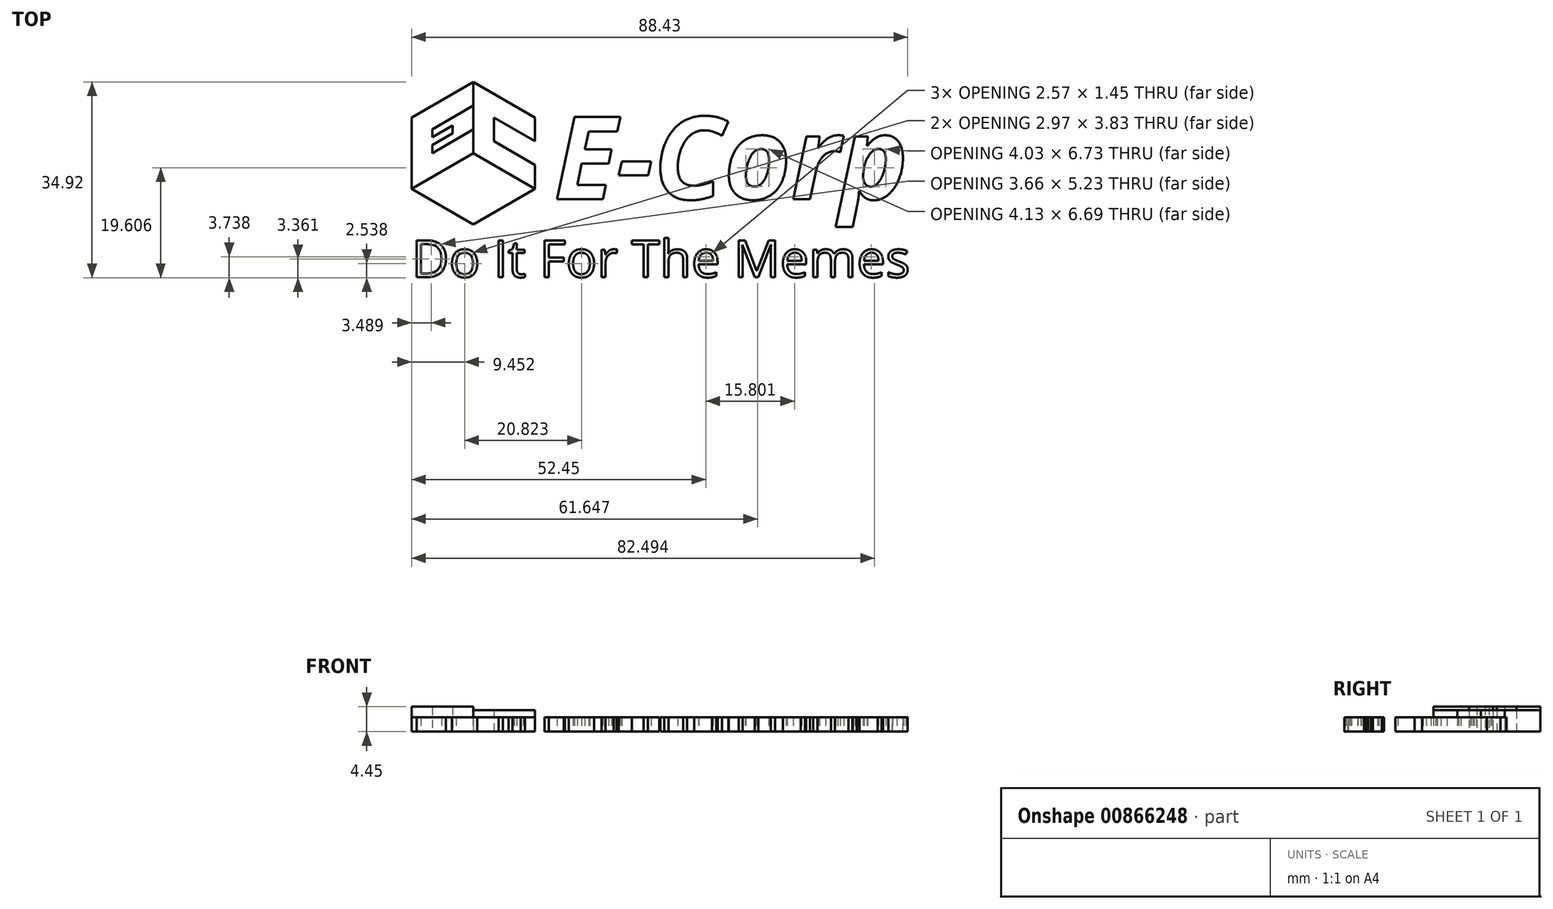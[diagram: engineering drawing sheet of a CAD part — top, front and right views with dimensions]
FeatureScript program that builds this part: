
annotation { "Feature Type Name" : "Feature", "Feature Type Description" : "" }
export const myFeature = defineFeature(function(context is Context, id is Id, definition is map)
    precondition{}
    {
        {
            var Q0;
            Q0=qCreatedBy(makeId("Top.planeOp"),FACE);
            var sketch = newSketch(context, id + "F0", { "sketchPlane" : qUnion([Q0])});
            skCircle(sketch, "E0.cCircle", {"center": v(-33.45, 15.53) * mm, "radius": 12.7 * mm, "construction": true});
            skLineSegment(sketch, "E0.0", {"start": v(-33.45, 28.23) * mm, "end": v(-22.45, 21.88) * mm});
            skLineSegment(sketch, "E0.1", {"start": v(-22.45, 21.88) * mm, "end": v(-22.45, 9.18) * mm});
            skLineSegment(sketch, "E0.2", {"start": v(-22.45, 9.18) * mm, "end": v(-33.45, 2.83) * mm});
            skLineSegment(sketch, "E0.3", {"start": v(-33.45, 2.83) * mm, "end": v(-44.45, 9.18) * mm});
            skLineSegment(sketch, "E0.4", {"start": v(-44.45, 9.18) * mm, "end": v(-44.45, 21.88) * mm});
            skLineSegment(sketch, "E0.5", {"start": v(-44.45, 21.88) * mm, "end": v(-33.45, 28.23) * mm});
            skText(sketch, "E1", { "text": "E-Corp", "fontName": "OpenSans-BoldItalic.ttf"});
            skText(sketch, "E2", { "text": "Do It For The Memes", "fontName": "OpenSans-Regular.ttf"});
            skLineSegment(sketch, "E3", {"start": v(-33.45, 15.53) * mm, "end": v(-44.45, 9.18) * mm});
            skLineSegment(sketch, "E4", {"start": v(-22.45, 9.18) * mm, "end": v(-33.45, 15.53) * mm});
            skLineSegment(sketch, "E5", {"start": v(-33.45, 15.53) * mm, "end": v(-33.45, 28.23) * mm});
            skLineSegment(sketch, "E6", {"start": v(-33.45, 19.76) * mm, "end": v(-40.78, 15.53) * mm});
            skLineSegment(sketch, "E7", {"start": v(-33.45, 19.76) * mm, "end": v(-33.45, 24) * mm});
            skLineSegment(sketch, "E8", {"start": v(-40.78, 19.76) * mm, "end": v(-33.45, 24) * mm});
            skLineSegment(sketch, "E9", {"start": v(-37.12, 13.41) * mm, "end": v(-40.78, 11.3) * mm});
            skLineSegment(sketch, "E10", {"start": v(-40.78, 15.53) * mm, "end": v(-40.78, 16.94) * mm});
            skPoint(sketch, "E11", {"position": v(-33.45, 21.88) * mm});
            skPoint(sketch, "E12", {"position": v(-38.95, 12.35) * mm});
            skLineSegment(sketch, "E13", {"start": v(-40.78, 18.35) * mm, "end": v(-37.12, 20.47) * mm});
            skLineSegment(sketch, "E14", {"start": v(-33.45, 22.58) * mm, "end": v(-33.45, 21.17) * mm});
            skLineSegment(sketch, "E15", {"start": v(-37.12, 19.06) * mm, "end": v(-40.78, 16.94) * mm});
            skLineSegment(sketch, "E16", {"start": v(-29.79, 17.64) * mm, "end": v(-29.79, 21.88) * mm});
            skLineSegment(sketch, "E17", {"start": v(-29.79, 26.11) * mm, "end": v(-26.12, 24) * mm});
            skLineSegment(sketch, "E18", {"start": v(-29.79, 21.88) * mm, "end": v(-22.45, 17.64) * mm});
            skLineSegment(sketch, "E19", {"start": v(-22.45, 17.64) * mm, "end": v(-22.45, 13.41) * mm});
            skLineSegment(sketch, "E20", {"start": v(-22.45, 13.41) * mm, "end": v(-29.79, 17.64) * mm});
            skPoint(sketch, "E21", {"position": v(-27.95, 25.05) * mm});
            skLineSegment(sketch, "E22.trimOffspring", {"start": v(-40.78, 18.35) * mm, "end": v(-40.78, 19.76) * mm});
            skLineSegment(sketch, "E23.trimOffspring", {"start": v(-37.12, 20.47) * mm, "end": v(-37.12, 19.06) * mm});
            const initialGuessF0  = {"E1": [-0.01905, 0.00732, 1, 0, 0.01476], "E2": [-0.04445, -0.0066, 1, 0, 0.0066]};
            skSetInitialGuess(sketch, initialGuessF0);
            skSolve(sketch);
        }
        {
            var Q0;
            {var subQ6=sQuery(id+"F0.wireOp",EDGE,"E0.4");Q0=makeQuery(id+"F0.imprint","IMPRINT",FACE,{"disambiguationData":[TD([[makeQuery(id+"F0.imprint","IMPRINT",EDGE,{"derivedFrom":subQ6}),-1.0]])]});}
            var Q1;
            {var subQ7=sQuery(id+"F0.wireOp",EDGE,"E4");Q1=makeQuery(id+"F0.imprint","IMPRINT",FACE,{"disambiguationData":[TD([[makeQuery(id+"F0.imprint","IMPRINT",EDGE,{"derivedFrom":subQ7}),-1.0]])]});}
            var Q2;
            Q2=makeQuery(id+"F0.imprint","IMPRINT",FACE,{"disambiguationData":[TD([[makeQuery(id+"F0.imprint","IMPRINT",EDGE,{"derivedFrom":sQuery(id+"F0.wireOp",EDGE,"E1.sketch_text.stroke-0")}),-1.0]])]});
            var Q3;
            Q3=makeQuery(id+"F0.imprint","IMPRINT",FACE,{"disambiguationData":[TD([[makeQuery(id+"F0.imprint","IMPRINT",EDGE,{"derivedFrom":sQuery(id+"F0.wireOp",EDGE,"E1.sketch_text.stroke-12")}),-1.0]])]});
            var Q4;
            Q4=makeQuery(id+"F0.imprint","IMPRINT",FACE,{"disambiguationData":[TD([[makeQuery(id+"F0.imprint","IMPRINT",EDGE,{"derivedFrom":sQuery(id+"F0.wireOp",EDGE,"E1.sketch_text.stroke-16")}),-1.0]])]});
            var Q5;
            Q5=makeQuery(id+"F0.imprint","IMPRINT",FACE,{"disambiguationData":[TD([[makeQuery(id+"F0.imprint","IMPRINT",EDGE,{"derivedFrom":sQuery(id+"F0.wireOp",EDGE,"E1.sketch_text.stroke-34")}),-1.0]])]});
            var Q6;
            Q6=makeQuery(id+"F0.imprint","IMPRINT",FACE,{"disambiguationData":[TD([[makeQuery(id+"F0.imprint","IMPRINT",EDGE,{"derivedFrom":sQuery(id+"F0.wireOp",EDGE,"E1.sketch_text.stroke-52")}),-1.0]])]});
            var Q7;
            Q7=makeQuery(id+"F0.imprint","IMPRINT",FACE,{"disambiguationData":[TD([[makeQuery(id+"F0.imprint","IMPRINT",EDGE,{"derivedFrom":sQuery(id+"F0.wireOp",EDGE,"E1.sketch_text.stroke-64")}),-1.0]])]});
            var Q8;
            Q8=makeQuery(id+"F0.imprint","IMPRINT",FACE,{"disambiguationData":[TD([[makeQuery(id+"F0.imprint","IMPRINT",EDGE,{"derivedFrom":sQuery(id+"F0.wireOp",EDGE,"E2.sketch_text.stroke-0")}),-1.0]])]});
            var Q9;
            Q9=makeQuery(id+"F0.imprint","IMPRINT",FACE,{"disambiguationData":[TD([[makeQuery(id+"F0.imprint","IMPRINT",EDGE,{"derivedFrom":sQuery(id+"F0.wireOp",EDGE,"E2.sketch_text.stroke-14")}),-1.0]])]});
            var Q10;
            Q10=makeQuery(id+"F0.imprint","IMPRINT",FACE,{"disambiguationData":[TD([[makeQuery(id+"F0.imprint","IMPRINT",EDGE,{"derivedFrom":sQuery(id+"F0.wireOp",EDGE,"E2.sketch_text.stroke-31")}),-1.0]])]});
            var Q11;
            Q11=makeQuery(id+"F0.imprint","IMPRINT",FACE,{"disambiguationData":[TD([[makeQuery(id+"F0.imprint","IMPRINT",EDGE,{"derivedFrom":sQuery(id+"F0.wireOp",EDGE,"E2.sketch_text.stroke-35")}),-1.0]])]});
            var Q12;
            Q12=makeQuery(id+"F0.imprint","IMPRINT",FACE,{"disambiguationData":[TD([[makeQuery(id+"F0.imprint","IMPRINT",EDGE,{"derivedFrom":sQuery(id+"F0.wireOp",EDGE,"E2.sketch_text.stroke-54")}),-1.0]])]});
            var Q13;
            Q13=makeQuery(id+"F0.imprint","IMPRINT",FACE,{"disambiguationData":[TD([[makeQuery(id+"F0.imprint","IMPRINT",EDGE,{"derivedFrom":sQuery(id+"F0.wireOp",EDGE,"E2.sketch_text.stroke-64")}),-1.0]])]});
            var Q14;
            Q14=makeQuery(id+"F0.imprint","IMPRINT",FACE,{"disambiguationData":[TD([[makeQuery(id+"F0.imprint","IMPRINT",EDGE,{"derivedFrom":sQuery(id+"F0.wireOp",EDGE,"E2.sketch_text.stroke-81")}),-1.0]])]});
            var Q15;
            Q15=makeQuery(id+"F0.imprint","IMPRINT",FACE,{"disambiguationData":[TD([[makeQuery(id+"F0.imprint","IMPRINT",EDGE,{"derivedFrom":sQuery(id+"F0.wireOp",EDGE,"E2.sketch_text.stroke-94")}),-1.0]])]});
            var Q16;
            Q16=makeQuery(id+"F0.imprint","IMPRINT",FACE,{"disambiguationData":[TD([[makeQuery(id+"F0.imprint","IMPRINT",EDGE,{"derivedFrom":sQuery(id+"F0.wireOp",EDGE,"E2.sketch_text.stroke-102")}),-1.0]])]});
            var Q17;
            Q17=makeQuery(id+"F0.imprint","IMPRINT",FACE,{"disambiguationData":[TD([[makeQuery(id+"F0.imprint","IMPRINT",EDGE,{"derivedFrom":sQuery(id+"F0.wireOp",EDGE,"E2.sketch_text.stroke-120")}),-1.0]])]});
            var Q18;
            Q18=makeQuery(id+"F0.imprint","IMPRINT",FACE,{"disambiguationData":[TD([[makeQuery(id+"F0.imprint","IMPRINT",EDGE,{"derivedFrom":sQuery(id+"F0.wireOp",EDGE,"E2.sketch_text.stroke-139")}),-1.0]])]});
            var Q19;
            Q19=makeQuery(id+"F0.imprint","IMPRINT",FACE,{"disambiguationData":[TD([[makeQuery(id+"F0.imprint","IMPRINT",EDGE,{"derivedFrom":sQuery(id+"F0.wireOp",EDGE,"E2.sketch_text.stroke-157")}),-1.0]])]});
            var Q20;
            Q20=makeQuery(id+"F0.imprint","IMPRINT",FACE,{"disambiguationData":[TD([[makeQuery(id+"F0.imprint","IMPRINT",EDGE,{"derivedFrom":sQuery(id+"F0.wireOp",EDGE,"E2.sketch_text.stroke-176")}),-1.0]])]});
            var Q21;
            Q21=makeQuery(id+"F0.imprint","IMPRINT",FACE,{"disambiguationData":[TD([[makeQuery(id+"F0.imprint","IMPRINT",EDGE,{"derivedFrom":sQuery(id+"F0.wireOp",EDGE,"E2.sketch_text.stroke-204")}),-1.0]])]});
            var Q22;
            Q22=makeQuery(id+"F0.imprint","IMPRINT",FACE,{"disambiguationData":[TD([[makeQuery(id+"F0.imprint","IMPRINT",EDGE,{"derivedFrom":sQuery(id+"F0.wireOp",EDGE,"E2.sketch_text.stroke-223")}),-1.0]])]});
            var Q23;
            Q23=makeQuery(id+"F0.imprint","IMPRINT",FACE,{"disambiguationData":[TD([[makeQuery(id+"F0.imprint","IMPRINT",EDGE,{"derivedFrom":sQuery(id+"F0.wireOp",EDGE,"E0.2")}),-1.0]])]});
            extrude(context, id + "F1", {"entities" : qUnion([Q0, Q1, Q2, Q3, Q4, Q5, Q6, Q7, Q8, Q9, Q10, Q11, Q12, Q13, Q14, Q15, Q16, Q17, Q18, Q19, Q20, Q21, Q22, Q23]), "depth" : 2.54 * mm, "offsetDistance" : 25.4 * mm});
        }
        {
            var Q0;
            {var subQ6=sQuery(id+"F0.wireOp",EDGE,"E0.4");Q0=makeQuery(id+"F0.imprint","IMPRINT",FACE,{"disambiguationData":[TD([[makeQuery(id+"F0.imprint","IMPRINT",EDGE,{"derivedFrom":subQ6}),-1.0]])]});}
            var Q1;
            {var subQ7=sQuery(id+"F0.wireOp",EDGE,"E4");Q1=makeQuery(id+"F0.imprint","IMPRINT",FACE,{"disambiguationData":[TD([[makeQuery(id+"F0.imprint","IMPRINT",EDGE,{"derivedFrom":subQ7}),-1.0]])]});}
            extrude(context, id + "F2", {"entities" : qUnion([Q0, Q1]), "operationType" : NewBodyOperationType.ADD, "depth" : 3.8 * mm, "offsetDistance" : 25.4 * mm});
        }
        {
            var Q0;
            {var subQ6=sQuery(id+"F0.wireOp",EDGE,"E0.4");Q0=makeQuery(id+"F0.imprint","IMPRINT",FACE,{"disambiguationData":[TD([[makeQuery(id+"F0.imprint","IMPRINT",EDGE,{"derivedFrom":subQ6}),-1.0]])]});}
            extrude(context, id + "F3", {"entities" : qUnion([Q0]), "operationType" : NewBodyOperationType.ADD, "depth" : 4.44 * mm, "offsetDistance" : 25.4 * mm});
        }
    });
